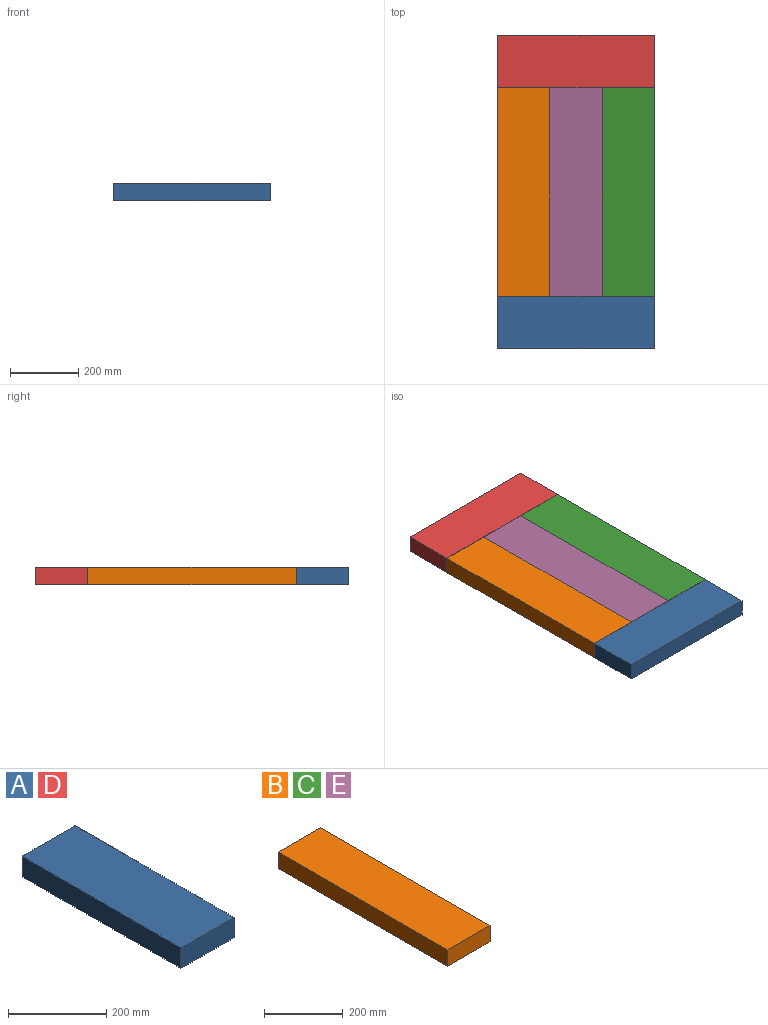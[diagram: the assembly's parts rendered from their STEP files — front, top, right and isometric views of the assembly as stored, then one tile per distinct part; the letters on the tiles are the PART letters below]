
ASSEMBLY  parts=5 mates=6
PART A: 6 faces, bbox 152.4x457.2x50.8 mm
  f0: plane 457.2x152.4mm, normal (0,0,1), area 69677.3mm2, adj f1,f3,f4,f5
  f1: plane 457.2x50.8mm, normal (-1,0,0), area 23225.8mm2, adj f0,f2,f4,f5
  f2: plane 457.2x152.4mm, normal (0,0,-1), area 69677.3mm2, adj f1,f3,f4,f5
  f3: plane 457.2x50.8mm, normal (1,0,0), area 23225.8mm2, adj f0,f2,f4,f5
  f4: plane 152.4x50.8mm, normal (0,-1,0), area 7741.9mm2, adj f0,f1,f2,f3
  f5: plane 152.4x50.8mm, normal (0,1,0), area 7741.9mm2, adj f0,f1,f2,f3
PART B: 6 faces, bbox 152.4x609.6x50.8 mm
  f0: plane 609.6x152.4mm, normal (0,0,1), area 92903mm2, adj f1,f3,f4,f5
  f1: plane 609.6x50.8mm, normal (-1,0,0), area 30967.7mm2, adj f0,f2,f4,f5
  f2: plane 609.6x152.4mm, normal (0,0,-1), area 92903mm2, adj f1,f3,f4,f5
  f3: plane 609.6x50.8mm, normal (1,0,0), area 30967.7mm2, adj f0,f2,f4,f5
  f4: plane 152.4x50.8mm, normal (0,-1,0), area 7741.9mm2, adj f0,f1,f2,f3
  f5: plane 152.4x50.8mm, normal (0,1,0), area 7741.9mm2, adj f0,f1,f2,f3
PART C: same geometry as B
PART D: same geometry as A
PART E: same geometry as B
PLACE A rot(axis=(0.71,0.71,0),180deg) t=(1052.57,-1130.28,-166.69)mm
PLACE B rot(axis=(0,0,1),180deg) t=(900.17,-749.28,-166.69)mm
PLACE C t=(1204.97,-749.28,-166.69)mm fixed
PLACE D rot(axis=(0,0,-1),90deg) t=(1052.57,-368.28,-166.69)mm
PLACE E t=(1052.57,-749.28,-166.69)mm
MATE planar C.f4 <-> E.f4  axis (0,-1,0) through (1204.97,-1054.08,-166.69)mm
MATE fastened A.f3 <-> E.f4  axis (0,1,0) through (1052.57,-1054.08,-166.69)mm
MATE planar C.f1 <-> E.f3  axis (-1,0,0) through (1128.77,-749.28,-166.69)mm
MATE fastened D.f3 <-> E.f5  axis (0,-1,0) through (1052.57,-444.48,-166.69)mm
MATE fastened B.f0 <-> E.f0  axis (0,0,1) through (900.17,-749.28,-141.29)mm
MATE planar E.f0 <-> C.f0  axis (0,0,1) through (1052.57,-749.28,-141.29)mm
